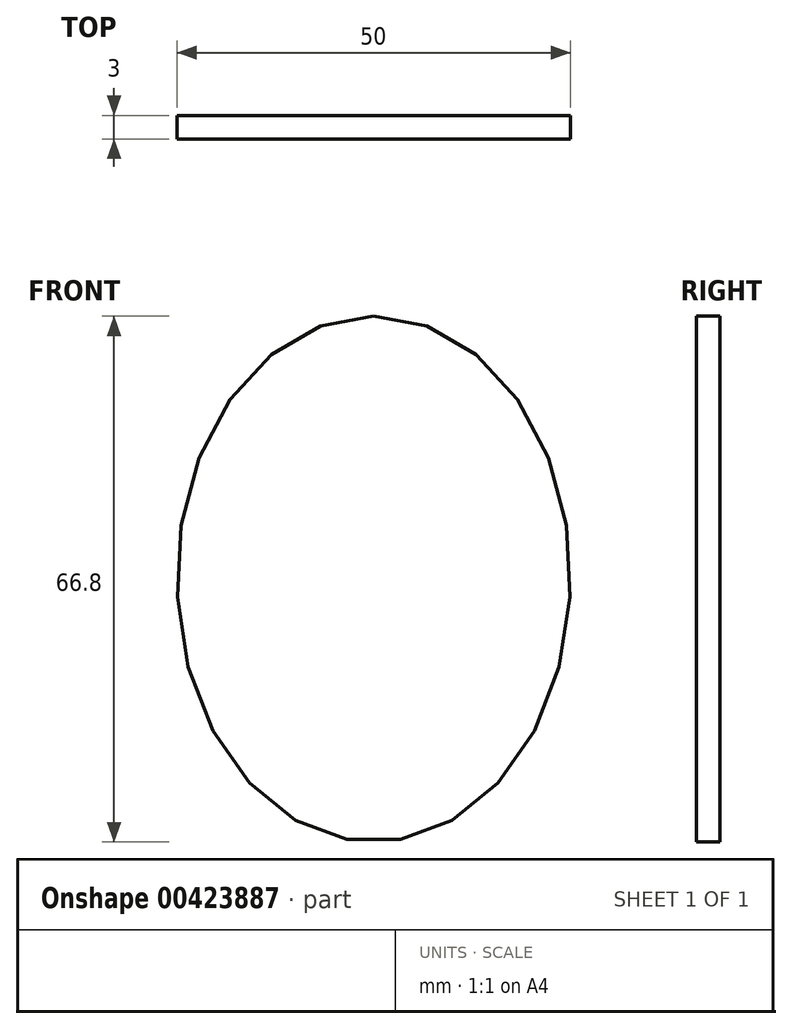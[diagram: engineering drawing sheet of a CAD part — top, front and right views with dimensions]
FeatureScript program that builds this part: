
annotation { "Feature Type Name" : "Feature", "Feature Type Description" : "" }
export const myFeature = defineFeature(function(context is Context, id is Id, definition is map)
    precondition{}
    {
        {
            var Q0;
            Q0=qCreatedBy(makeId("Front.planeOp"),FACE);
            var sketch = newSketch(context, id + "F0", { "sketchPlane" : qUnion([Q0])});
            skEllipse(sketch, "E0", {"center": v(0, 0) * mm, "majorRadius": 33.4 * mm, "minorRadius": 25 * mm, "majorAxis": v(0, 1)});
            skSolve(sketch);
        }
        {
            var Q0;
            Q0=makeQuery(id+"F0.imprint","IMPRINT",FACE,{"disambiguationData":[TD([[makeQuery(id+"F0.imprint","IMPRINT",EDGE,{"derivedFrom":sQuery(id+"F0.wireOp",EDGE,"E0")}),1.0]])]});
            extrude(context, id + "F1", {"entities" : qUnion([Q0]), "depth" : 3 * mm});
        }
    });
